# Revit family: EWD
name_source: partatom
category: Mechanical Equipment
units: mm (PartAtom-declared; Revit-internal decimal feet)

## family parameters
Always vertical = Yes
Cut with Voids When Loaded = No
Part Type = Normal
Room Calculation Point = No
Round Connector Dimension = Use Diameter
Shared = No
Work Plane-Based = No

## types (6) — shared parameters
-D = -3"
.125 = 1/8"
.5" = 1/2"
0 = 0"
1" = 1"
1.5 = 1 1/2"
2" = 2"
2' = 24"
3" = 3"
4" = 4"
9" = 9"
E = 3"
E/2 = 1 1/2"
Manufacturer = Loren Cook Company
Model = EWD
Type Comments = Wall Exhaust Fan Extruded Aluminum Propeller Direct Drive
URL = www.lorencook.com
WH_ANGLE = 130.00°
WH_ANGLE_2 = 92.00°

## per-type parameters (varying)
- 24_EWD: (A/2)-1"=17 27/32"; (A/2)-C-.5"=10 19/32"; (D_SUP/2)-(C/2)-.125"=11 3/8"; (SIZE/2)-.25"=11 3/4"; -((A/2)-C-.5")=-10 19/32"; -((SIZE/2)-.25")=-11 3/4"; -B=-14 5/8"; -B+1"=-13 5/8"; -C/2=-3 1/2"; -WC_D=-18 11/16"; -WG_A=-20 9/16"; -WH_B/2=-20"; A=36 3/16"; A/2=18 3/32"; A/3.5=10 11/32"; A/7=5 5/32"; B=14 5/8"; B/2=7 5/16"; C=7"; C/2=3 1/2"; D=30"; D/2=15"; WC_A=36 1/4"; WC_B=39 9/16"; WC_C=34 7/16"; WG_B=37"; WG_D=12 9/16"; WH_A=31 7/16"; WH_B=40"; WH_B/2=20"; WO=36 7/16"
- 30_EWD: (A/2)-1"=20 27/32"; (A/2)-C-.5"=13 25/32"; (D_SUP/2)-(C/2)-.125"=14 15/32"; (SIZE/2)-.25"=14 3/4"; -((A/2)-C-.5")=-13 25/32"; -((SIZE/2)-.25")=-14 3/4"; -B=-14 5/8"; -B+1"=-13 5/8"; -C/2=-3 13/32"; -WC_D=-19 7/16"; -WG_A=-20 9/16"; -WH_B/2=-23"; A=42 3/16"; A/2=21 3/32"; A/3.5=12 1/16"; A/7=6 1/32"; B=14 5/8"; B/2=7 5/16"; C=6 13/16"; C/2=3 13/32"; D=36"; D/2=18"; WC_A=42 1/4"; WC_B=45 9/16"; WC_C=40 1/2"; WG_B=43"; WG_D=12 9/16"; WH_A=35 11/16"; WH_B=46"; WH_B/2=23"; WO=42 7/16"
- 36_EWD: (A/2)-1"=23 27/32"; (A/2)-C-.5"=16 11/32"; (D_SUP/2)-(C/2)-.125"=17 1/4"; (SIZE/2)-.25"=17 3/4"; -((A/2)-C-.5")=-16 11/32"; -((SIZE/2)-.25")=-17 3/4"; -B=-22"; -B+1"=-21"; -C/2=-3 5/8"; -WC_D=-19 7/16"; -WG_A=-25 9/16"; -WH_B/2=-26"; A=48 3/16"; A/2=24 3/32"; A/3.5=13 25/32"; A/7=6 7/8"; B=22"; B/2=11"; C=7 1/4"; C/2=3 5/8"; D=42"; D/2=21"; WC_A=48 1/4"; WC_B=51 5/8"; WC_C=46 1/2"; WG_B=49"; WG_D=12 9/16"; WH_A=39 15/16"; WH_B=52"; WH_B/2=26"; WO=48 7/16"
- 42_EWD: (A/2)-1"=26 27/32"; (A/2)-C-.5"=18 31/32"; (D_SUP/2)-(C/2)-.125"=20 1/16"; (SIZE/2)-.25"=20 3/4"; -((A/2)-C-.5")=-18 31/32"; -((SIZE/2)-.25")=-20 3/4"; -B=-24"; -B+1"=-23"; -C/2=-3 13/16"; -WC_D=-19 11/16"; -WG_A=-28 7/16"; -WH_B/2=-29"; A=54 3/16"; A/2=27 3/32"; A/3.5=15 15/32"; A/7=7 3/4"; B=24"; B/2=12"; C=7 5/8"; C/2=3 13/16"; D=48"; D/2=24"; WC_A=54 1/4"; WC_B=57 5/8"; WC_C=52 1/2"; WG_B=55"; WG_D=13 7/16"; WH_A=44 3/16"; WH_B=58"; WH_B/2=29"; WO=54 7/16"
- 48_EWD: (A/2)-1"=29 27/32"; (A/2)-C-.5"=21 27/32"; (D_SUP/2)-(C/2)-.125"=23"; (SIZE/2)-.25"=23 3/4"; -((A/2)-C-.5")=-21 27/32"; -((SIZE/2)-.25")=-23 3/4"; -B=-24"; -B+1"=-23"; -C/2=-3 7/8"; -WC_D=-19 11/16"; -WG_A=-28 7/16"; -WH_B/2=-32"; A=60 3/16"; A/2=30 3/32"; A/3.5=17 3/16"; A/7=8 19/32"; B=24"; B/2=12"; C=7 3/4"; C/2=3 7/8"; D=54"; D/2=27"; WC_A=60 1/4"; WC_B=63 11/16"; WC_C=58 9/16"; WG_B=61"; WG_D=13 7/16"; WH_A=48 7/16"; WH_B=64"; WH_B/2=32"; WO=60 7/16"
- 54_EWD: (A/2)-1"=32 27/32"; (A/2)-C-.5"=24 29/32"; (D_SUP/2)-(C/2)-.125"=26 1/32"; (SIZE/2)-.25"=23 3/4"; -((A/2)-C-.5")=-24 29/32"; -((SIZE/2)-.25")=-23 3/4"; -B=-27 3/4"; -B+1"=-26 3/4"; -C/2=-3 27/32"; -WC_D=-19 11/16"; -WG_A=-28 7/16"; -WH_B/2=-35"; A=66 3/16"; A/2=33 3/32"; A/3.5=18 29/32"; A/7=9 15/32"; B=27 3/4"; B/2=13 7/8"; C=7 11/16"; C/2=3 27/32"; D=60"; D/2=30"; WC_A=66 1/4"; WC_B=69 11/16"; WC_C=64 9/16"; WG_B=67"; WG_D=13 7/16"; WH_A=52 5/8"; WH_B=70"; WH_B/2=35"; WO=66 7/16"

## geometry (parser evidence)
native form markers: Sweep x2
no freeform markers — native parametric forms only
